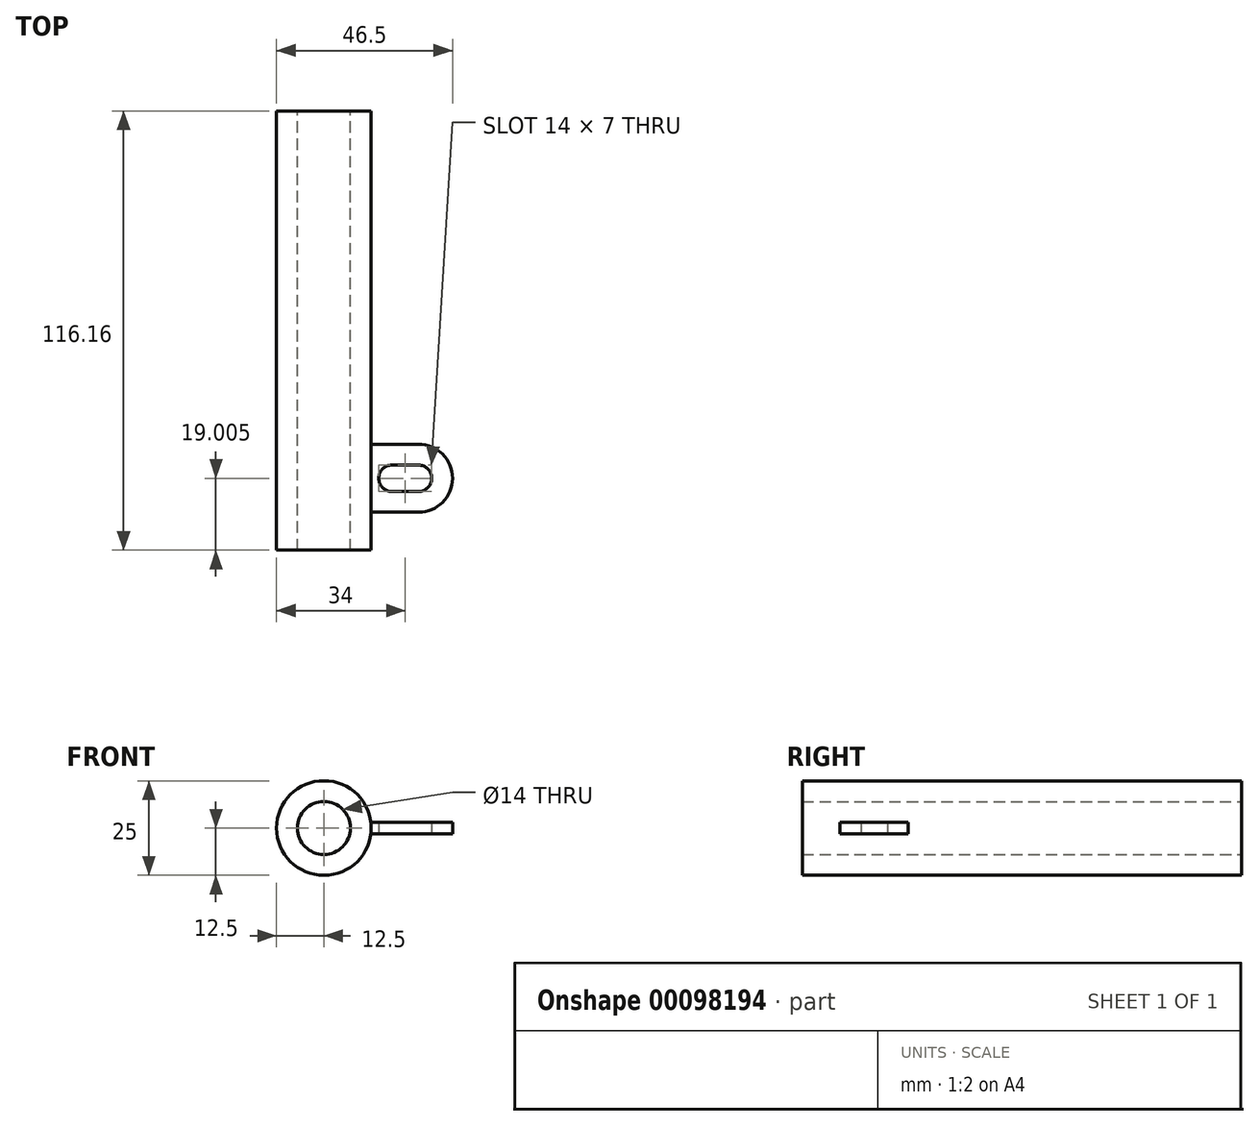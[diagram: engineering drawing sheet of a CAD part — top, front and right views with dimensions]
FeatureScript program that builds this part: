
annotation { "Feature Type Name" : "Feature", "Feature Type Description" : "" }
export const myFeature = defineFeature(function(context is Context, id is Id, definition is map)
    precondition{}
    {
        {
            var Q0;
            Q0=qCreatedBy(makeId("Front.planeOp"),FACE);
            var sketch = newSketch(context, id + "F0", { "sketchPlane" : qUnion([Q0])});
            skCircle(sketch, "E0", {"center": v(0, 0) * mm, "radius": 12.5 * mm});
            skCircle(sketch, "E1", {"center": v(0, 0) * mm, "radius": 7 * mm});
            skSolve(sketch);
        }
        {
            var Q0;
            Q0=qSketchRegion(id+"F0",true);
            extrude(context, id + "F1", {"entities" : qUnion([Q0]), "endBound" : BoundingType.SYMMETRIC, "depth" : (180 - 63.85) * mm});
        }
        {
            var Q0;
            Q0=qCreatedBy(makeId("Top.planeOp"),FACE);
            var sketch = newSketch(context, id + "F2", { "sketchPlane" : qUnion([Q0])});
            skLineSegment(sketch, "E2", {"start": v(10, -48.08) * mm, "end": v(25, -48.08) * mm});
            skLineSegment(sketch, "E3", {"start": v(25, -30.07) * mm, "end": v(10, -30.07) * mm});
            skLineSegment(sketch, "E4", {"start": v(10, -30.08) * mm, "end": v(10, -48.08) * mm});
            skArc(sketch, "E5", {"start": v(25, -48.07) * mm, "mid": v(34, -39.07) * mm, "end": v(25, -30.07) * mm});
            skArc(sketch, "E6", {"start": v(25, -35.57) * mm, "mid": v(28.5, -39.07) * mm, "end": v(25, -42.57) * mm});
            skLineSegment(sketch, "E7", {"start": v(25, -42.57) * mm, "end": v(18, -42.57) * mm});
            skLineSegment(sketch, "E8", {"start": v(25, -35.57) * mm, "end": v(18, -35.57) * mm});
            skArc(sketch, "E9", {"start": v(18, -42.57) * mm, "mid": v(14.5, -39.07) * mm, "end": v(18, -35.57) * mm});
            skSolve(sketch);
        }
        {
            var Q0;
            Q0=qSketchRegion(id+"F2",true);
            extrude(context, id + "F3", {"entities" : qUnion([Q0]), "operationType" : NewBodyOperationType.ADD, "endBound" : BoundingType.SYMMETRIC, "depth" : 3 * mm});
        }
    });
